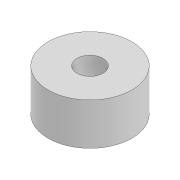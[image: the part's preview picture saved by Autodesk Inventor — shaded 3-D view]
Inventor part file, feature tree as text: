
AUTODESK INVENTOR PART (.ipt)
format: ipt  version: 2022 (Build 260153000, 153)  size: 82,944 bytes
history: native  units: mm
features: extrude x1, sketch x1
ambient origin geometry x8: Origin, YZ Plane, XZ Plane, XY Plane, X Axis, Y Axis, Z Axis, Center Point
bodies: Solid1 (feature_tree)
feature tree (2):
  extrude  "Extrusion1"  Depth=10.0mm
  sketch  "Sketch1"  dims[d0=3.1mm d1=10.0mm d2=5.0mm d3=0.0mm]
